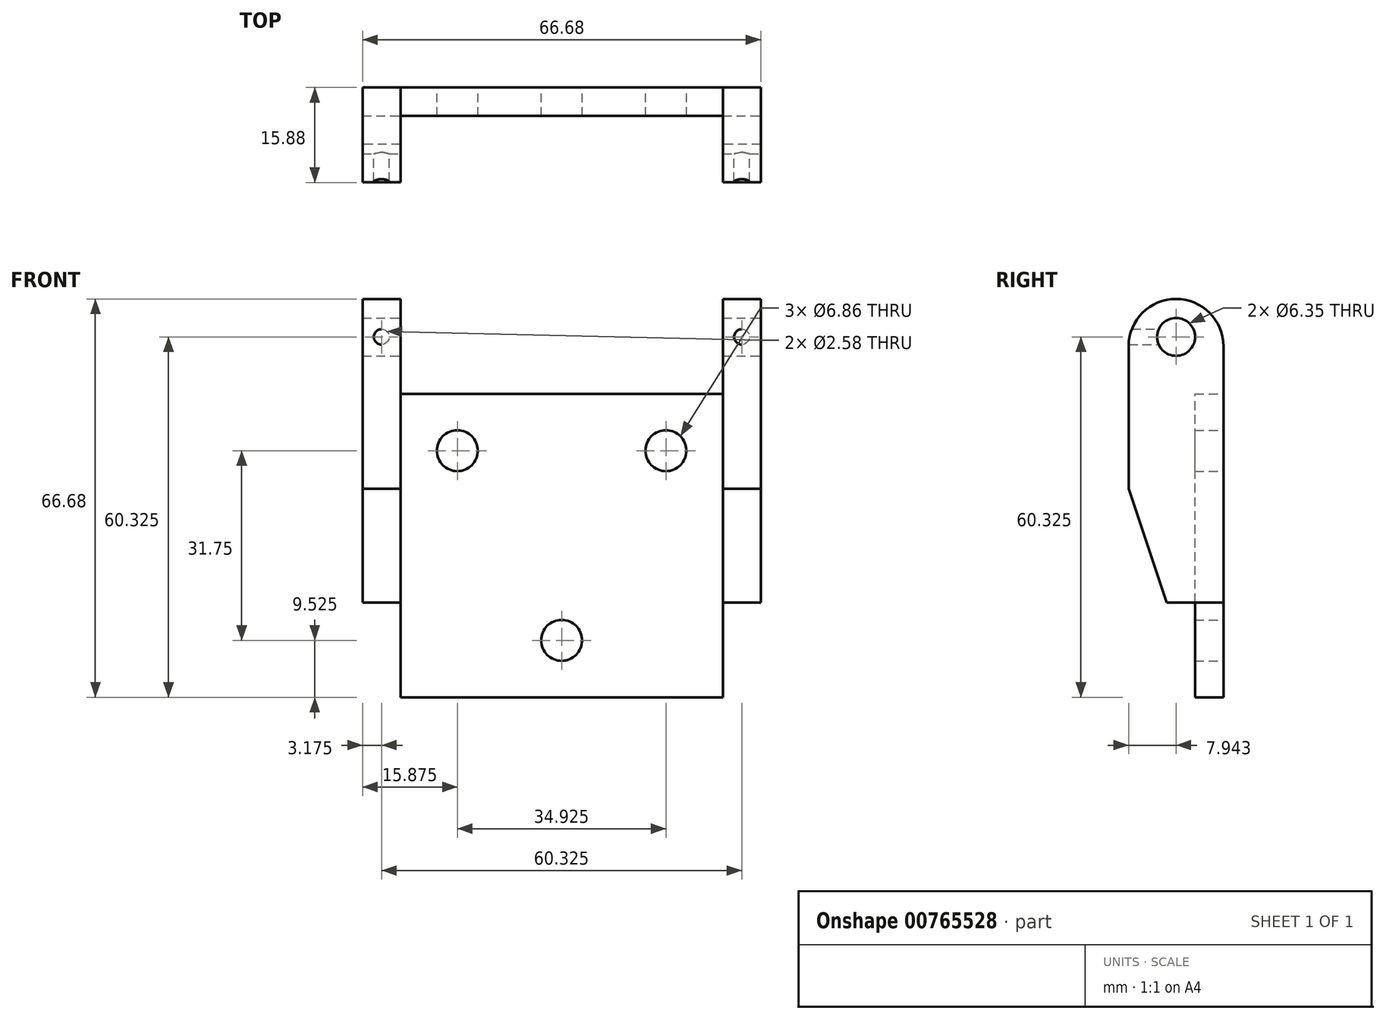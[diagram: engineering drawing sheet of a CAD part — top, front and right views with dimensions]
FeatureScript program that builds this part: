
annotation { "Feature Type Name" : "Feature", "Feature Type Description" : "" }
export const myFeature = defineFeature(function(context is Context, id is Id, definition is map)
    precondition{}
    {
        {
            var Q0;
            Q0=qCreatedBy(makeId("Front.planeOp"),FACE);
            var sketch = newSketch(context, id + "F0", { "sketchPlane" : qUnion([Q0])});
            skLineSegment(sketch, "E0.bottom", {"start": v(0, 0) * mm, "end": v(53.98, 0) * mm});
            skLineSegment(sketch, "E0.top", {"start": v(0, 50.8) * mm, "end": v(53.97, 50.8) * mm});
            skLineSegment(sketch, "E0.left", {"start": v(0, 0) * mm, "end": v(0, 50.8) * mm});
            skLineSegment(sketch, "E0.right", {"start": v(53.98, 0) * mm, "end": v(53.97, 50.8) * mm});
            skCircle(sketch, "E1", {"center": v(9.52, 41.28) * mm, "radius": 3.43 * mm});
            skCircle(sketch, "E2", {"center": v(44.45, 41.28) * mm, "radius": 3.43 * mm});
            skCircle(sketch, "E3", {"center": v(26.99, 9.53) * mm, "radius": 3.43 * mm});
            skLineSegment(sketch, "E4", {"start": v(9.52, 44.7) * mm, "end": v(44.45, 44.7) * mm, "construction": true});
            skPoint(sketch, "E5", {"position": v(26.99, 44.7) * mm});
            skLineSegment(sketch, "E6", {"start": v(9.52, 37.85) * mm, "end": v(44.45, 37.85) * mm, "construction": true});
            skPoint(sketch, "E7", {"position": v(26.99, 37.85) * mm});
            skSolve(sketch);
        }
        {
            var Q0;
            Q0=makeQuery(id+"F0.imprint","IMPRINT",FACE,{"disambiguationData":[TD([[makeQuery(id+"F0.imprint","IMPRINT",EDGE,{"derivedFrom":sQuery(id+"F0.wireOp",EDGE,"E0.bottom")}),1.0]])]});
            extrude(context, id + "F1", {"entities" : qUnion([Q0]), "depth" : 4.76 * mm, "offsetDistance" : 25.4 * mm});
        }
        {
            var Q0;
            Q0=qCreatedBy(makeId("Front.planeOp"),FACE);
            var sketch = newSketch(context, id + "F2", { "sketchPlane" : qUnion([Q0])});
            skLineSegment(sketch, "E8.bottom", {"start": v(0, 15.88) * mm, "end": v(-6.35, 15.88) * mm});
            skLineSegment(sketch, "E8.top", {"start": v(0, 66.68) * mm, "end": v(-6.35, 66.68) * mm});
            skLineSegment(sketch, "E8.left", {"start": v(0, 15.88) * mm, "end": v(0, 66.68) * mm});
            skLineSegment(sketch, "E8.right", {"start": v(-6.35, 15.88) * mm, "end": v(-6.35, 66.68) * mm});
            skLineSegment(sketch, "E9.bottom", {"start": v(53.97, 15.88) * mm, "end": v(60.32, 15.88) * mm});
            skLineSegment(sketch, "E9.top", {"start": v(53.97, 66.68) * mm, "end": v(60.32, 66.68) * mm});
            skLineSegment(sketch, "E9.left", {"start": v(53.97, 15.88) * mm, "end": v(53.97, 66.68) * mm});
            skLineSegment(sketch, "E9.right", {"start": v(60.32, 15.88) * mm, "end": v(60.32, 66.68) * mm});
            skSolve(sketch);
        }
        {
            var Q0;
            Q0 = qSketchRegion(id + "F2", true);
            extrude(context, id + "F3", {"entities" : qUnion([Q0]), "operationType" : NewBodyOperationType.ADD, "depth" : 15.88 * mm, "offsetDistance" : 25.4 * mm});
        }
        {
            var Q0;
            Q0=qCreatedBy(makeId("Right.planeOp"),FACE);
            var sketch = newSketch(context, id + "F4", { "sketchPlane" : qUnion([Q0])});
            skCircle(sketch, "E10", {"center": v(-7.94, 60.33) * mm, "radius": 3.18 * mm});
            skSolve(sketch);
        }
        {
            var Q0;
            Q0 = qSketchRegion(id + "F4", true);
            extrude(context, id + "F5", {"entities" : qUnion([Q0]), "operationType" : NewBodyOperationType.REMOVE, "endBound" : BoundingType.UP_TO_NEXT, "oppositeDirection" : true, "depth" : 25.4 * mm, "offsetDistance" : 25.4 * mm});
        }
        {
            var Q0;
            Q0=makeQuery(id+"F3.opExtrude","SWEPT_FACE",FACE,{"disambiguationData":[OSD([sQuery(id+"F2.wireOp",EDGE,"E9.right")])]});
            var sketch = newSketch(context, id + "F6", { "sketchPlane" : qUnion([Q0])});
            skCircle(sketch, "E11", {"center": v(-7.94, 60.32) * mm, "radius": 3.18 * mm});
            skSolve(sketch);
        }
        {
            var Q0;
            Q0 = qSketchRegion(id + "F6", true);
            extrude(context, id + "F7", {"entities" : qUnion([Q0]), "operationType" : NewBodyOperationType.REMOVE, "oppositeDirection" : true, "depth" : 6.35 * mm, "offsetDistance" : 25.4 * mm});
        }
        {
            var Q0;
            Q0=makeQuery(id+"F3.opExtrude","CAP_FACE",FACE,{"disambiguationData":[OSD([sQuery(id+"F2.wireOp",EDGE,"E8.bottom"),sQuery(id+"F2.wireOp",EDGE,"E8.top"),sQuery(id+"F2.wireOp",EDGE,"E8.left"),sQuery(id+"F2.wireOp",EDGE,"E8.right")])],"isStart":false});
            var sketch = newSketch(context, id + "F8", { "sketchPlane" : qUnion([Q0])});
            skCircle(sketch, "E12", {"center": v(-3.18, 60.33) * mm, "radius": 1.29 * mm});
            skLineSegment(sketch, "E13.0", {"start": v(0, 50.8) * mm, "end": v(53.97, 50.8) * mm, "construction": true});
            skLineSegment(sketch, "E14", {"start": v(26.99, 50.8) * mm, "end": v(26.99, 80.36) * mm, "construction": true});
            skCircle(sketch, "E15.MirrorC", {"center": v(57.15, 60.33) * mm, "radius": 1.29 * mm});
            skSolve(sketch);
        }
        {
            var Q0;
            Q0=sQuery(id+"F8.wireOp",VERTEX,"E12.center");
            var Q1;
            Q1=sQuery(id+"F8.wireOp",VERTEX,"E15.MirrorC.center");
            var Q2;
            Q2=makeQuery(id+"F1.opExtrude","SWEPT_BODY",BODY,{"disambiguationData":[OSD([sQuery(id+"F0.wireOp",EDGE,"E0.bottom"),sQuery(id+"F0.wireOp",EDGE,"E0.top"),sQuery(id+"F0.wireOp",EDGE,"E0.left"),sQuery(id+"F0.wireOp",EDGE,"E0.right"),sQuery(id+"F0.wireOp",EDGE,"E1"),sQuery(id+"F0.wireOp",EDGE,"E2"),sQuery(id+"F0.wireOp",EDGE,"E3")])]});
            hole(context, id + "F9", {"style" : HoleStyle.SIMPLE, "endStyle" : HoleEndStyle.BLIND, "standardTappedOrClearance" : lookupTablePath({ "standard" : "ANSI", "engagement" : "75%", "pitch" : "40 tpi", "size" : "#5", "type" : "Tapped" }), "standardBlindInLast" : lookupTablePath({ "standard" : "ANSI", "engagement" : "75%", "pitch" : "40 tpi", "size" : "#5", "type" : "Tapped" }), "holeDiameter" : 2.58 * mm, "majorDiameter" : 3.17 * mm, "showTappedDepth" : true, "holeDepth" : 7.94 * mm, "isTappedThrough" : true, "tappedDepth" : 7.94 * mm, "tapClearance" : 0, "locations" : qUnion([Q0, Q1]), "scope" : qUnion([Q2])});
        }
        {
            var Q0;
            Q0=makeQuery(id+"F3.opExtrude","CAP_EDGE",EDGE,{"disambiguationData":[OSD([sQuery(id+"F2.wireOp",EDGE,"E9.top")])],"isStart":false});
            var Q1;
            Q1=makeQuery(id+"F3.opExtrude","CAP_EDGE",EDGE,{"disambiguationData":[OSD([sQuery(id+"F2.wireOp",EDGE,"E9.top")])],"isStart":true});
            var Q2;
            Q2=makeQuery(id+"F3.opExtrude","CAP_EDGE",EDGE,{"disambiguationData":[OSD([sQuery(id+"F2.wireOp",EDGE,"E8.top")])],"isStart":false});
            var Q3;
            Q3=makeQuery(id+"F3.opExtrude","CAP_EDGE",EDGE,{"disambiguationData":[OSD([sQuery(id+"F2.wireOp",EDGE,"E8.top")])],"isStart":true});
            fillet(context, id + "F10", {"entities" : qUnion([Q0, Q1, Q2, Q3]), "radius" : 7.94 * mm, "tangentPropagation" : true, "allowEdgeOverflow" : false});
        }
        {
            var Q0;
            Q0=makeQuery(id+"F3.opExtrude","CAP_EDGE",EDGE,{"disambiguationData":[OSD([sQuery(id+"F2.wireOp",EDGE,"E8.bottom")])],"isStart":false});
            chamfer(context, id + "F11", {"entities" : qUnion([Q0]), "chamferType" : ChamferType.TWO_OFFSETS, "width1" : 6.35 * mm, "oppositeDirection" : false, "width2" : 19.05 * mm, "tangentPropagation" : true});
        }
        {
            var Q0;
            Q0=makeQuery(id+"F3.opExtrude","CAP_EDGE",EDGE,{"disambiguationData":[OSD([sQuery(id+"F2.wireOp",EDGE,"E9.bottom")])],"isStart":false});
            chamfer(context, id + "F12", {"entities" : qUnion([Q0]), "chamferType" : ChamferType.TWO_OFFSETS, "width1" : 6.35 * mm, "oppositeDirection" : true, "width2" : 19.05 * mm, "tangentPropagation" : true});
        }
    });
